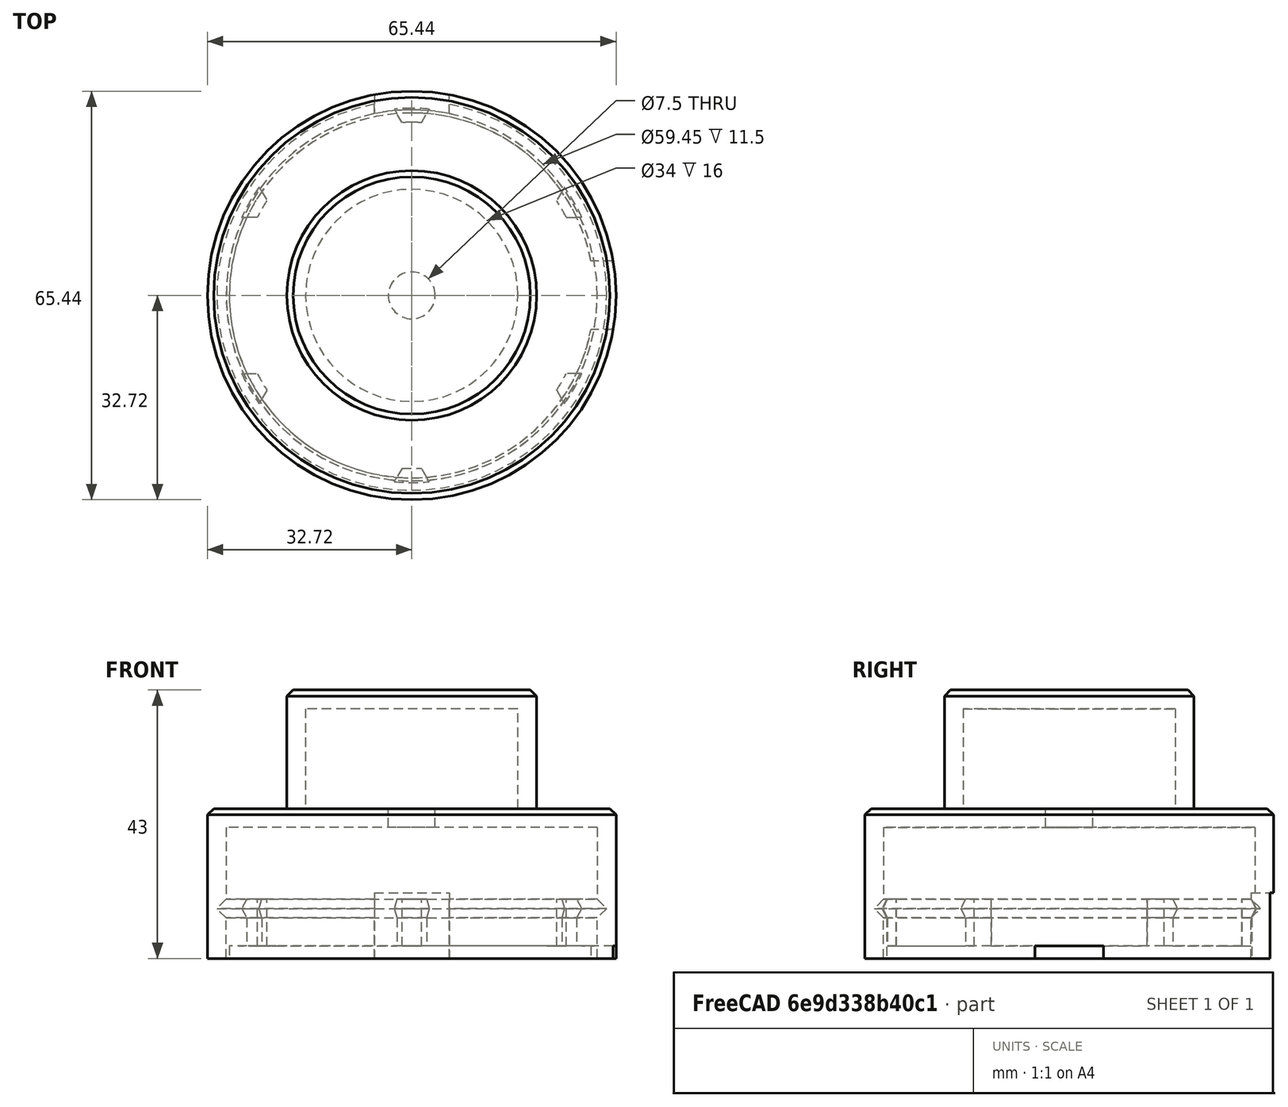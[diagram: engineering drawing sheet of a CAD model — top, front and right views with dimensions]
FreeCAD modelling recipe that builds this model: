
FCSTD DOCUMENT  (FreeCAD 0.17R13541 (Git))
Label: LightController
License: All rights reserved
LicenseURL: http://en.wikipedia.org/wiki/All_rights_reserved
objects: Sketcher::SketchObject×7, PartDesign::Pocket×3, PartDesign::Body×3, App::Part×3, PartDesign::Pad×2, PartDesign::Revolution×2, PartDesign::Chamfer×2, Spreadsheet::Sheet×1, Mesh::Feature×1
note: 26 computed .brp shape members not serialized (recipe doc carries the construction recipe); baked Part::Feature solids carry a one-line shape summary decoded from their .brp

FEATURE [Sketcher::SketchObject] Sketch
  MapMode = 5
  Support = -> [XY_Plane001]
  expr: Constraints[1] = D.WRad
  sketch-geometry (1):
    g0: Circle CenterX=0 CenterY=0 CenterZ=0 NormalX=0 NormalY=0 NormalZ=1 AngleXU=0 Radius=20
  constraints (2):
    c: Coincident(g0,g-1)
    c: Radius(g0) = 20
FEATURE [Spreadsheet::Sheet] Spreadsheet  label="D"
  cells = B2=Offset; C2(Offset)==0.25mm; B3=Wall Thiccness; C3(WThic)==3mm; A4=Wheel; B4=Diameter; C4==40mm; B5=Radius; C5(WRad)==C4 / 2; B6=Height; C6(WHeight)==19mm; B7=Edge; C7(WEdge)==3mm; A8=Rot enc; B8=Hole Dia; C8==7mm; B9=Hole Radius; C9(RotR)==C8 / 2 + Offset; A10=Boards; B10=Board W; C10==28.5mm; B11=Board H; C11==51.600000000000001mm; B12=Board dia; C12==sqrt(C10 ^ 2 + C11 ^ 2); A13=Container; B13=Container radius; C13(ConRad)==C12 / 2 + Offset; B14=Container Height; C14(ConHei)==18mm; B15=BotHei; B16=Lip Height; C16(LipH)==5mm; B17=Lip cutout; C17(LipCut)==25mm; B18=Cable Con W; C18(CabW)==12mm; B19=Cable Con H; C19(CabH)==7.5mm
FEATURE [PartDesign::Pad] Pad
  Length = 19
  Length2 = 100
  Profile = -> Sketch
  Type = 0
  expr: Length = D.WHeight
FEATURE [Sketcher::SketchObject] Sketch001
  MapMode = 5
  Placement = pos=(0,0,0) rot=(1,0,0;3.14159rad)
  Support = -> [Pad]
  expr: Constraints[1] = D.WRad - D.WEdge
  sketch-geometry (1):
    g0: Circle CenterX=0 CenterY=0 CenterZ=0 NormalX=0 NormalY=0 NormalZ=1 AngleXU=0 Radius=17
  constraints (2):
    c: Coincident(g0,g-1)
    c: Radius(g0) = 17
FEATURE [PartDesign::Pocket] Pocket
  BaseFeature = -> Pad
  Length = 16
  Length2 = 100
  Profile = -> Sketch001
  Type = 0
  expr: Length = D.WHeight - D.WEdge
FEATURE [Sketcher::SketchObject] Sketch002
  MapMode = 5
  Placement = pos=(0,0,0) rot=(1,0,0;1.5708rad)
  Support = -> [XZ_Plane003]
  expr: Constraints[26] = D.ConRad
  expr: Constraints[22] = D.LipH + D.WThic
  expr: Constraints[9] = D.WThic
  expr: Constraints[23] = D.WThic / 2
  expr: Constraints[21] = D.WThic
  expr: Constraints[10] = D.WThic
  expr: Constraints[11] = D.ConHei + D.WThic
  expr: Constraints[8] = D.RotR
  sketch-geometry (9):
    g0: LineSegment StartX=32.7238 StartY=0 StartZ=0 EndX=32.7238 EndY=-24 EndZ=0
    g1: LineSegment StartX=32.7238 StartY=-24 StartZ=0 EndX=29.7238 EndY=-24 EndZ=0
    g2: LineSegment StartX=29.7238 StartY=-3 StartZ=0 EndX=3.75 EndY=-3 EndZ=0
    g3: LineSegment StartX=3.75 StartY=-3 StartZ=0 EndX=3.75 EndY=0 EndZ=0
    g4: LineSegment StartX=29.7238 StartY=-24 StartZ=0 EndX=29.7238 EndY=-17.5 EndZ=0
    g5: LineSegment StartX=29.7238 StartY=-3 StartZ=0 EndX=29.7238 EndY=-14.5 EndZ=0
    g6: LineSegment StartX=29.7238 StartY=-14.5 StartZ=0 EndX=31.2238 EndY=-16 EndZ=0
    g7: LineSegment StartX=31.2238 StartY=-16 StartZ=0 EndX=29.7238 EndY=-17.5 EndZ=0
    g8: LineSegment StartX=3.75 StartY=0 StartZ=0 EndX=32.7238 EndY=0 EndZ=0
  constraints (27):
    c: PointOnObject(g0,g-1)
    c: Vertical(g0)
    c: Coincident(g1,g0)
    c: Horizontal(g1)
    c: Horizontal(g2)
    c: Coincident(g3,g2)
    c: PointOnObject(g3,g-1)
    c: Vertical(g3)
    c: DistanceX(g-1,g3) = 3.75
    c: DistanceY(g2,g3) = 3
    c: DistanceX(g1,g0) = 3
    c: DistanceY(g1,g2) = 21
    c: Coincident(g4,g1)
    c: Vertical(g4)
    c: Coincident(g5,g2)
    c: Vertical(g5)
    c: Coincident(g6,g5)
    c: Coincident(g7,g6)
    c: Coincident(g7,g4)
    c: Angle(g6,g7) = 1.5708
    c: Angle(g4,g7) = 2.35619
    c: DistanceX(g2,g0) = 3
    c: DistanceY(g0,g6) = 8
    c: DistanceX(g4,g6) = 1.5
    c: Coincident(g8,g3)
    c: Coincident(g8,g0)
    c: DistanceX(g-1,g2) = 29.7238
FEATURE [PartDesign::Revolution] Revolution
  Angle = 360
  Axis = (0,0,1)
  Base = (0,0,0)
  Placement = pos=(0,0,0) rot=(1,0,0;1.5708rad)
  Profile = -> Sketch002
  ReferenceAxis = -> Sketch002 [V_Axis]
FEATURE [PartDesign::Chamfer] Chamfer
  Base = -> Revolution [Edge5]
  BaseFeature = -> Revolution
  Placement = pos=(0,0,0) rot=(1,0,0;1.5708rad)
  Size = 1
FEATURE [PartDesign::Chamfer] Chamfer001
  Base = -> Pocket [Edge3]
  BaseFeature = -> Pocket
  Size = 1
FEATURE [PartDesign::Body] Body
  Group = -> [Sketch,Pad,Sketch001,Pocket,Chamfer001]
  Origin = -> Origin001
  Tip = -> Chamfer001
FEATURE [App::Part] Part  label="Wheel"
  Group = -> [Body]
  License = CC BY 3.0
  LicenseURL = http://creativecommons.org/licenses/by/3.0/
  Origin = -> Origin
FEATURE [Sketcher::SketchObject] Sketch003
  MapMode = 5
  Placement = pos=(0,2e-12,-24) rot=(1,0,0;3.14159rad)
  Support = -> [Chamfer]
  expr: Constraints[11] = D.CabW / 2
  expr: Constraints[8] = D.CabW
  sketch-geometry (5):
    g0: LineSegment StartX=6 StartY=-50 StartZ=0 EndX=-6 EndY=-50 EndZ=0
    g1: LineSegment StartX=-6 StartY=-50 StartZ=0 EndX=-6 EndY=0 EndZ=0
    g2: LineSegment StartX=-6 StartY=0 StartZ=0 EndX=6 EndY=0 EndZ=0
    g3: LineSegment StartX=6 StartY=0 StartZ=0 EndX=6 EndY=-50 EndZ=0
    g4: GeomPoint X=0 Y=-50 Z=0
  constraints (14):
    c: Coincident(g0,g1)
    c: Coincident(g1,g2)
    c: Coincident(g2,g3)
    c: Coincident(g3,g0)
    c: Horizontal(g0)
    c: Horizontal(g2)
    c: Vertical(g1)
    c: Vertical(g3)
    c: DistanceX(g0,g0) = 12
    c: PointOnObject(g4,g0)
    c: PointOnObject(g4,g-2)
    c: DistanceX(g0,g4) = 6
    c: PointOnObject(g-1,g2)
    c: DistanceY(g4,g-1) = 50
FEATURE [PartDesign::Pocket] Pocket001
  BaseFeature = -> Chamfer
  Length = 10.5
  Length2 = 100
  Placement = pos=(0,0,0) rot=(1,0,0;1.5708rad)
  Profile = -> Sketch003
  Type = 0
  expr: Length = D.WThic + D.CabH
FEATURE [PartDesign::Body] Body001  label="Container001"
  Group = -> [Sketch002,Revolution,Chamfer,Sketch003,Pocket001]
  Origin = -> Origin003
  Tip = -> Pocket001
FEATURE [App::Part] Part001  label="Container"
  Group = -> [Body001]
  License = CC BY 3.0
  LicenseURL = http://creativecommons.org/licenses/by/3.0/
  Origin = -> Origin002
FEATURE [Sketcher::SketchObject] Sketch004
  MapMode = 5
  Placement = pos=(0,0,0) rot=(0.57735,0.57735,0.57735;2.0944rad)
  Support = -> [YZ_Plane005]
  expr: Constraints[21] = D.WThic / 2
  expr: Constraints[20] = D.WThic / 2
  expr: Constraints[23] = D.LipH + D.WThic / 3 * 1
  expr: Constraints[19] = D.WThic / 4
  expr: Constraints[18] = D.WThic / 2
  expr: Constraints[22] = D.ConHei + D.WThic + D.WThic / 3 * 1
  expr: Constraints[17] = D.WThic / 3 * 2
  expr: Constraints[9] = D.WThic / 2
  expr: Constraints[10] = D.ConRad - D.Offset * 2
  sketch-geometry (8):
    g0: LineSegment StartX=0 StartY=-22 StartZ=0 EndX=27.7238 EndY=-22 EndZ=0
    g1: LineSegment StartX=27.7238 StartY=-22 StartZ=0 EndX=27.7238 EndY=-14.5 EndZ=0
    g2: LineSegment StartX=29.9738 StartY=-16 StartZ=0 EndX=29.2238 EndY=-17.5 EndZ=0
    g3: LineSegment StartX=29.2238 StartY=-17.5 StartZ=0 EndX=29.2238 EndY=-24 EndZ=0
    g4: LineSegment StartX=29.2238 StartY=-24 StartZ=0 EndX=0 EndY=-24 EndZ=0
    g5: LineSegment StartX=27.7238 StartY=-14.5 StartZ=0 EndX=29.2238 EndY=-14.5 EndZ=0
    g6: LineSegment StartX=29.9738 StartY=-16 StartZ=0 EndX=29.2238 EndY=-14.5 EndZ=0
    g7: LineSegment StartX=0 StartY=-22 StartZ=0 EndX=0 EndY=-24 EndZ=0
  constraints (24):
    c: PointOnObject(g0,g-2)
    c: Horizontal(g0)
    c: Coincident(g1,g0)
    c: Vertical(g1)
    c: Coincident(g3,g2)
    c: Vertical(g3)
    c: Coincident(g4,g3)
    c: PointOnObject(g4,g-2)
    c: Horizontal(g4)
    c: DistanceX(g0,g3) = 1.5
    c: Distance(g4) = 29.2238
    c: Coincident(g5,g1)
    c: Horizontal(g5)
    c: Coincident(g6,g2)
    c: Coincident(g6,g5)
    c: Coincident(g7,g0)
    c: Coincident(g7,g4)
    c: DistanceY(g4,g0) = 2
    c: DistanceY(g2,g2) = 1.5
    c: DistanceX(g2,g2) = 0.75
    c: DistanceY(g2,g5) = 1.5
    c: Distance(g5) = 1.5
    c: Distance(g-1,g0) = 22
    c: DistanceY(g0,g2) = 6
FEATURE [PartDesign::Revolution] Revolution001
  Angle = 360
  Axis = (0,0,1)
  Base = (0,0,0)
  Placement = pos=(0,0,0) rot=(0.57735,0.57735,0.57735;2.0944rad)
  Profile = -> Sketch004
  ReferenceAxis = -> Sketch004 [V_Axis]
FEATURE [Sketcher::SketchObject] Sketch005
  MapMode = 5
  Placement = pos=(2e-12,-2e-12,-14.5) rot=(0,0,-1;1.5708rad)
  Support = -> [Revolution001]
  expr: Constraints[35] = D.ConRad + D.WThic / 2
  expr: Constraints[34] = D.ConRad + D.WThic / 2
  expr: Constraints[27] = D.LipCut / 2
  expr: Constraints[22] = D.LipCut
  expr: Constraints[31] = D.ConRad + D.WThic / 2
  expr: Constraints[25] = D.LipCut / 2
  expr: Constraints[21] = D.LipCut
  expr: Constraints[32] = D.ConRad + D.WThic / 2
  expr: Constraints[26] = D.ConRad + D.WThic / 2
  expr: Constraints[24] = D.LipCut / 2
  expr: Constraints[33] = D.ConRad + D.WThic / 2
  expr: Constraints[20] = D.LipCut
  sketch-geometry (29):
    g0: LineSegment [constr] StartX=-12.5 StartY=31.2238 StartZ=0 EndX=-12.5 EndY=-31.2238 EndZ=0
    g1: LineSegment StartX=-12.5 StartY=31.2238 StartZ=0 EndX=12.5 EndY=31.2238 EndZ=0
    g2: LineSegment [constr] StartX=12.5 StartY=31.2238 StartZ=0 EndX=12.5 EndY=-31.2238 EndZ=0
    g3: LineSegment [constr] StartX=-20.7906 StartY=26.4372 StartZ=0 EndX=33.2906 EndY=-4.78656 EndZ=0
    g4: LineSegment StartX=-20.7906 StartY=26.4372 StartZ=0 EndX=-33.2906 EndY=4.78656 EndZ=0
    g5: LineSegment [constr] StartX=20.7906 StartY=26.4372 StartZ=0 EndX=-33.2906 EndY=-4.78656 EndZ=0
    g6: LineSegment StartX=-33.2906 StartY=-4.78656 StartZ=0 EndX=-20.7906 EndY=-26.4372 EndZ=0
    g7: LineSegment [constr] StartX=-20.7906 StartY=-26.4372 StartZ=0 EndX=33.2906 EndY=4.78656 EndZ=0
    g8: LineSegment StartX=33.2906 StartY=4.78656 StartZ=0 EndX=20.7906 EndY=26.4372 EndZ=0
    g9: LineSegment StartX=33.2906 StartY=-4.78656 StartZ=0 EndX=20.7906 EndY=-26.4372 EndZ=0
    g10: LineSegment [constr] StartX=20.7906 StartY=-26.4372 StartZ=0 EndX=-33.2906 EndY=4.78656 EndZ=0
    g11: LineSegment StartX=-12.5 StartY=-31.2238 StartZ=0 EndX=12.5 EndY=-31.2238 EndZ=0
    g12: GeomPoint X=-25 Y=0 Z=0
    g13: GeomPoint X=-12.5 Y=-21.6506 Z=0
    g14: GeomPoint X=25 Y=0 Z=0
    g15: GeomPoint X=12.5 Y=21.6506 Z=0
    g16: GeomPoint X=-12.5 Y=21.6506 Z=0
    g17: LineSegment StartX=-20.7906 StartY=26.4372 StartZ=0 EndX=-12.5 EndY=21.6506 EndZ=0
    g18: LineSegment StartX=-12.5 StartY=21.6506 StartZ=0 EndX=-12.5 EndY=31.2238 EndZ=0
    g19: LineSegment StartX=12.5 StartY=31.2238 StartZ=0 EndX=12.5 EndY=21.6506 EndZ=0
    g20: LineSegment StartX=12.5 StartY=21.6506 StartZ=0 EndX=20.7906 EndY=26.4372 EndZ=0
    g21: LineSegment StartX=33.2906 StartY=4.78656 StartZ=0 EndX=25 EndY=0 EndZ=0
    g22: LineSegment StartX=25 StartY=0 StartZ=0 EndX=33.2906 EndY=-4.78656 EndZ=0
    g23: LineSegment StartX=-25 StartY=0 StartZ=0 EndX=-33.2906 EndY=4.78656 EndZ=0
    g24: LineSegment StartX=-25 StartY=0 StartZ=0 EndX=-33.2906 EndY=-4.78656 EndZ=0
    g25: LineSegment StartX=-20.7906 StartY=-26.4372 StartZ=0 EndX=-12.5 EndY=-21.6506 EndZ=0
    g26: LineSegment StartX=-12.5 StartY=-21.6506 StartZ=0 EndX=-12.5 EndY=-31.2238 EndZ=0
    g27: LineSegment StartX=12.5 StartY=-31.2238 StartZ=0 EndX=12.5 EndY=-21.6506 EndZ=0
    g28: LineSegment StartX=12.5 StartY=-21.6506 StartZ=0 EndX=20.7906 EndY=-26.4372 EndZ=0
  constraints (71):
    c: Vertical(g0)
    c: Coincident(g1,g0)
    c: Horizontal(g1)
    c: Coincident(g2,g1)
    c: Vertical(g2)
    c: Coincident(g4,g3)
    c: Coincident(g6,g5)
    c: Coincident(g7,g6)
    c: Coincident(g8,g7)
    c: Coincident(g8,g5)
    c: Perpendicular(g3,g4)
    c: Perpendicular(g5,g8)
    c: Perpendicular(g6,g7)
    c: Angle(g0,g3) = 1.0472
    c: Coincident(g9,g3)
    c: Coincident(g10,g9)
    c: Coincident(g10,g4)
    c: Perpendicular(g10,g9)
    c: Perpendicular(g9,g3)
    c: Perpendicular(g7,g8)
    c: Distance(g1) = 25
    c: Distance(g8) = 25
    c: Distance(g4) = 25
    c: Angle(g5,g2) = 1.0472
    c: Distance(g-1,g5) = 12.5
    c: Distance(g-1,g3) = 12.5
    c: Distance(g-1,g1) = 31.2238
    c: Distance(g-1,g0) = 12.5
    c: Coincident(g11,g0)
    c: Coincident(g11,g2)
    c: Horizontal(g11)
    c: Distance(g-1,g11) = 31.2238
    c: Distance(g-1,g8) = 31.2238
    c: Distance(g-1,g6) = 31.2238
    c: Distance(g-1,g9) = 31.2238
    c: Distance(g-1,g4) = 31.2238
    c: PointOnObject(g12,g5)
    c: PointOnObject(g13,g0)
    c: PointOnObject(g14,g7)
    c: PointOnObject(g15,g2)
    c: PointOnObject(g16,g3)
    c: PointOnObject(g16,g0)
    c: PointOnObject(g12,g10)
    c: PointOnObject(g13,g7)
    c: PointOnObject(g14,g3)
    c: PointOnObject(g15,g5)
    c: Coincident(g17,g3)
    c: Coincident(g17,g16)
    c: Coincident(g18,g16)
    c: Coincident(g18,g0)
    c: Coincident(g19,g1)
    c: Coincident(g19,g15)
    c: Coincident(g20,g15)
    c: Coincident(g20,g5)
    c: Coincident(g21,g7)
    c: Coincident(g21,g14)
    c: Coincident(g22,g14)
    c: Coincident(g22,g3)
    c: Coincident(g23,g12)
    c: Coincident(g23,g4)
    c: Coincident(g24,g12)
    c: Coincident(g24,g5)
    c: Coincident(g25,g6)
    c: Coincident(g25,g13)
    c: Coincident(g26,g13)
    c: Coincident(g26,g0)
    c: Coincident(g27,g2)
    c: Coincident(g28,g27)
    c: Coincident(g28,g9)
    c: PointOnObject(g27,g10)
    c: PointOnObject(g27,g2)
FEATURE [PartDesign::Pocket] Pocket002
  BaseFeature = -> Revolution001
  Length = 7.5
  Length2 = 100
  Placement = pos=(0,0,0) rot=(0.57735,0.57735,0.57735;2.0944rad)
  Profile = -> Sketch005
  Type = 0
  expr: Length = D.LipH + D.WThic / 2 + D.WThic / 3 * 1
FEATURE [Sketcher::SketchObject] Sketch006
  MapMode = 5
  Placement = pos=(3e-12,-3e-12,-24) rot=(0.707107,0.707107,0;3.14159rad)
  Support = -> [Pocket002]
  expr: Constraints[13] = D.ConRad + D.WThic
  expr: Constraints[12] = (D.CabW - D.Offset * 4) / 2
  expr: Constraints[9] = D.CabW - D.Offset * 4
  sketch-geometry (5):
    g0: ArcOfCircle CenterX=0 CenterY=0 CenterZ=0 NormalX=0 NormalY=0 NormalZ=1 AngleXU=0 Radius=32.7238 StartAngle=1.40192 EndAngle=1.73967
    g1: LineSegment StartX=-5.5 StartY=32.2582 StartZ=0 EndX=-5.5 EndY=0 EndZ=0
    g2: LineSegment StartX=5.5 StartY=32.2582 StartZ=0 EndX=5.5 EndY=0 EndZ=0
    g3: LineSegment StartX=5.5 StartY=0 StartZ=0 EndX=-5.5 EndY=0 EndZ=0
    g4: GeomPoint X=0 Y=32.7238 Z=0
  constraints (14):
    c: Coincident(g0,g-1)
    c: Coincident(g1,g0)
    c: PointOnObject(g1,g-1)
    c: Vertical(g1)
    c: Coincident(g2,g0)
    c: PointOnObject(g2,g-1)
    c: Vertical(g2)
    c: Coincident(g3,g2)
    c: Coincident(g3,g1)
    c: DistanceX(g0,g0) = 11
    c: PointOnObject(g4,g0)
    c: PointOnObject(g4,g-2)
    c: DistanceX(g-1,g2) = 5.5
    c: DistanceY(g-1,g4) = 32.7238
FEATURE [PartDesign::Pad] Pad001
  BaseFeature = -> Pocket002
  Length = 2
  Length2 = 100
  Placement = pos=(0,0,0) rot=(0.57735,0.57735,0.57735;2.0944rad)
  Profile = -> Sketch006
  Reversed = true
  Type = 0
  expr: Length = D.WThic / 3 * 2
FEATURE [PartDesign::Body] Body002  label="Container Lid001"
  Group = -> [Sketch004,Revolution001,Sketch005,Pocket002,Sketch006,Pad001]
  Origin = -> Origin005
  Tip = -> Pad001
FEATURE [App::Part] Part002  label="Container Lid"
  Group = -> [Body002]
  License = CC BY 3.0
  LicenseURL = http://creativecommons.org/licenses/by/3.0/
  Origin = -> Origin004
  Placement = pos=(0,0,0) rot=(0,0,1;1.5708rad)
FEATURE [Mesh::Feature] Mesh  label="Container Lid001 (Meshed)"
